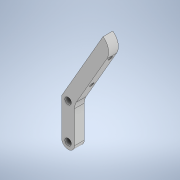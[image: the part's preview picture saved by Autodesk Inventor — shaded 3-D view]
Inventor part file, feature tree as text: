
AUTODESK INVENTOR PART (.ipt)
format: ipt  version: 2021 (Build 250183000, 183)  size: 143,360 bytes
history: native  units: mm
features: extrude x2, sketch x2, fillet x1
ambient origin geometry x8: Origin, YZ Plane, XZ Plane, XY Plane, X Axis, Y Axis, Z Axis, Center Point
bodies: Solid1 (feature_tree)
feature tree (5):
  extrude  "Extrusion1"  Depth=8.0mm
  fillet  "Fillet1"  Radius=22.0mm
  extrude  "Extrusion2"  Depth=8.0mm
  sketch  "Sketch1"  dims[d0=4.0mm d1=8.0mm d2=22.0mm]
  sketch  "Sketch2"  dims[d3=4.0mm d4=8.0mm d5=50.0mm d6=150.0deg d7=4.0mm d8=8.0mm d9=6.0mm d10=0.0mm d11=8.0mm d13=8.0mm d15=2.5mm d16=2.5mm d17=10.0mm d19=43.0mm d20=10.0mm d21=10.0mm d22=0.0mm]
